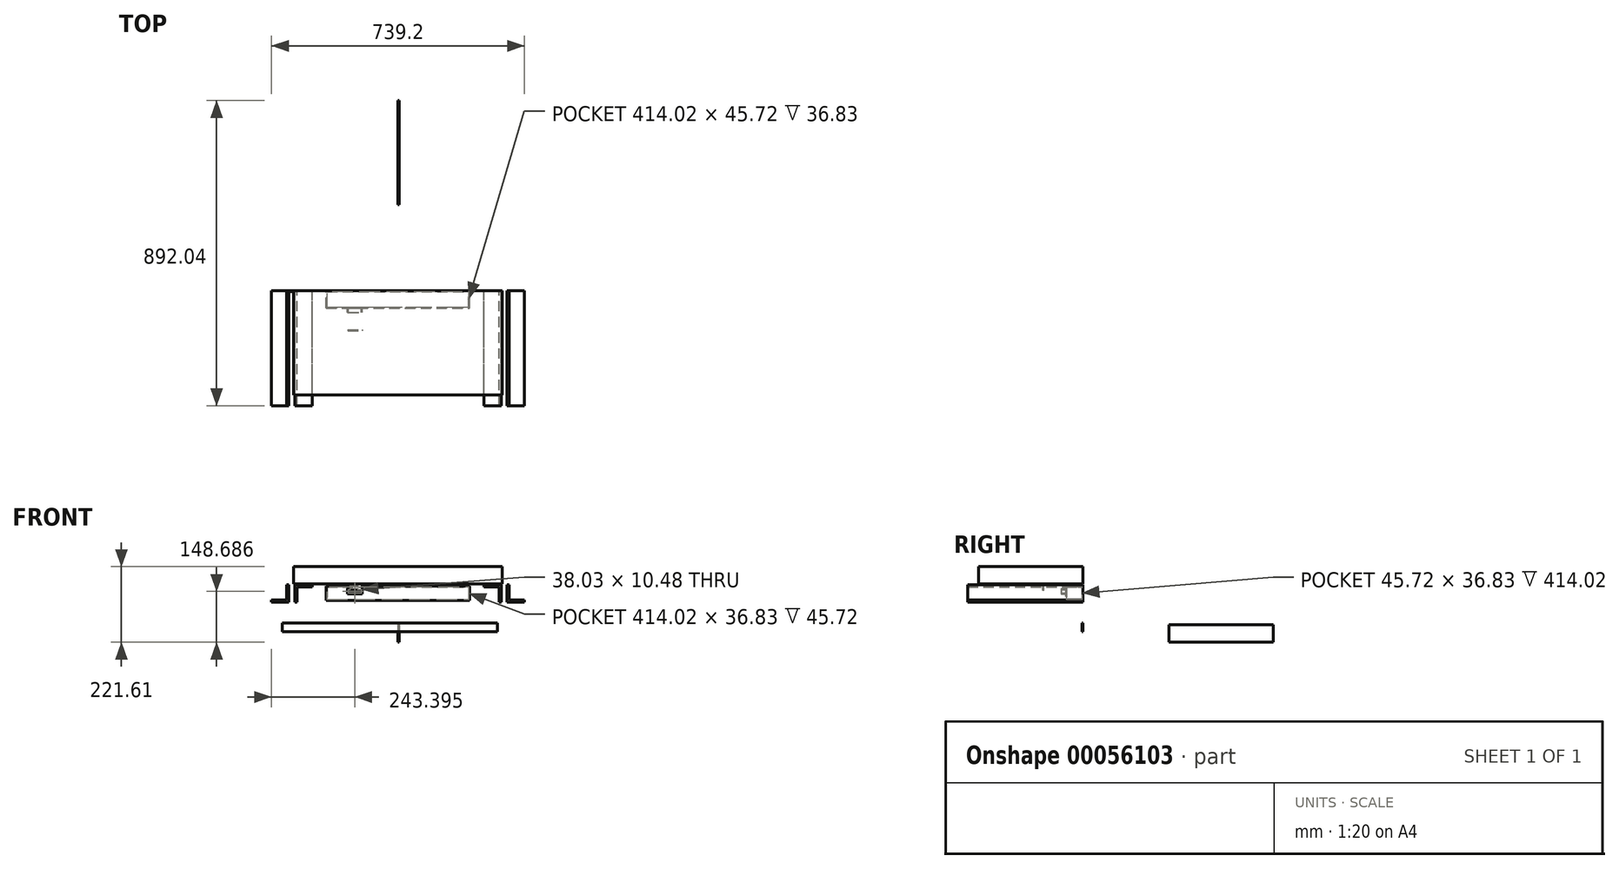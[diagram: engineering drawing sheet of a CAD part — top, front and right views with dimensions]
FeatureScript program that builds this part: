
annotation { "Feature Type Name" : "Feature", "Feature Type Description" : "" }
export const myFeature = defineFeature(function(context is Context, id is Id, definition is map)
    precondition{}
    {
        {
            var Q0;
            Q0=qCreatedBy(makeId("Front.planeOp"),FACE);
            var sketch = newSketch(context, id + "F0", { "sketchPlane" : qUnion([Q0])});
            skLineSegment(sketch, "E0.bottom", {"start": v(-304.8, 110.14) * mm, "end": v(304.8, 110.14) * mm});
            skLineSegment(sketch, "E0.top", {"start": v(-304.8, 59.34) * mm, "end": v(304.8, 59.34) * mm});
            skLineSegment(sketch, "E0.left", {"start": v(-304.8, 110.14) * mm, "end": v(-304.8, 59.34) * mm});
            skLineSegment(sketch, "E0.right", {"start": v(304.8, 110.14) * mm, "end": v(304.8, 59.34) * mm});
            skLineSegment(sketch, "E1.bottom", {"start": v(-209.55, 53) * mm, "end": v(209.55, 53) * mm});
            skLineSegment(sketch, "E1.top", {"start": v(-209.55, 11.08) * mm, "end": v(209.55, 11.08) * mm});
            skLineSegment(sketch, "E1.left", {"start": v(-209.55, 53) * mm, "end": v(-209.55, 11.08) * mm});
            skLineSegment(sketch, "E1.right", {"start": v(209.55, 53) * mm, "end": v(209.55, 11.08) * mm});
            skLineSegment(sketch, "E2", {"start": v(0, 0) * mm, "end": v(0, 201) * mm, "construction": true});
            skLineSegment(sketch, "E3", {"start": v(397.2, 0) * mm, "end": v(-209.55, 0) * mm, "construction": true});
            skSolve(sketch);
        }
        {
            var Q0;
            Q0=makeQuery(id+"F0.imprint","IMPRINT",FACE,{"disambiguationData":[TD([[makeQuery(id+"F0.imprint","IMPRINT",EDGE,{"derivedFrom":sQuery(id+"F0.wireOp",EDGE,"E1.bottom")}),-1.0]])]});
            extrude(context, id + "F1", {"entities" : qUnion([Q0]), "depth" : 50.8 * mm});
        }
        {
            var Q0;
            Q0=makeQuery(id+"F0.imprint","IMPRINT",FACE,{"disambiguationData":[TD([[makeQuery(id+"F0.imprint","IMPRINT",EDGE,{"derivedFrom":sQuery(id+"F0.wireOp",EDGE,"E0.bottom")}),-1.0]])]});
            extrude(context, id + "F2", {"entities" : qUnion([Q0]), "depth" : 304.8 * mm});
        }
        {
            var Q0;
            Q0=qCreatedBy(makeId("Front.planeOp"),FACE);
            var sketch = newSketch(context, id + "F3", { "sketchPlane" : qUnion([Q0])});
            skLineSegment(sketch, "E4", {"start": v(-342.89, 0) * mm, "end": v(465.36, 0) * mm, "construction": true});
            skLineSegment(sketch, "E5", {"start": v(0, -121.63) * mm, "end": v(0, 322.71) * mm, "construction": true});
            skLineSegment(sketch, "E6", {"start": v(250.8, 57.32) * mm, "end": v(301.6, 57.32) * mm});
            skLineSegment(sketch, "E7", {"start": v(301.6, 57.32) * mm, "end": v(301.6, 6.52) * mm});
            skLineSegment(sketch, "E8", {"start": v(301.6, 6.52) * mm, "end": v(295.24, 6.52) * mm});
            skLineSegment(sketch, "E9", {"start": v(295.24, 6.52) * mm, "end": v(295.24, 50.97) * mm});
            skLineSegment(sketch, "E10", {"start": v(295.24, 50.97) * mm, "end": v(250.8, 50.97) * mm});
            skLineSegment(sketch, "E11", {"start": v(250.8, 50.97) * mm, "end": v(250.8, 57.32) * mm});
            skLineSegment(sketch, "E12", {"start": v(318.8, 57.32) * mm, "end": v(318.8, 6.52) * mm});
            skLineSegment(sketch, "E13", {"start": v(318.8, 6.52) * mm, "end": v(369.6, 6.52) * mm});
            skLineSegment(sketch, "E14", {"start": v(369.6, 6.52) * mm, "end": v(369.6, 12.87) * mm});
            skLineSegment(sketch, "E15", {"start": v(369.6, 12.87) * mm, "end": v(325.15, 12.87) * mm});
            skLineSegment(sketch, "E16", {"start": v(325.15, 12.87) * mm, "end": v(325.15, 57.32) * mm});
            skLineSegment(sketch, "E17", {"start": v(325.15, 57.32) * mm, "end": v(318.8, 57.32) * mm});
            skLineSegment(sketch, "E18.MirrorCS", {"start": v(-325.15, 57.32) * mm, "end": v(-318.8, 57.32) * mm});
            skLineSegment(sketch, "E19.MirrorCS", {"start": v(-250.8, 50.97) * mm, "end": v(-250.8, 57.32) * mm});
            skLineSegment(sketch, "E20.MirrorCS", {"start": v(-325.15, 12.87) * mm, "end": v(-325.15, 57.32) * mm});
            skLineSegment(sketch, "E21.MirrorCS", {"start": v(-250.8, 57.32) * mm, "end": v(-301.6, 57.32) * mm});
            skLineSegment(sketch, "E22.MirrorCS", {"start": v(-301.6, 57.32) * mm, "end": v(-301.6, 6.52) * mm});
            skLineSegment(sketch, "E23.MirrorCS", {"start": v(-318.8, 57.32) * mm, "end": v(-318.8, 6.52) * mm});
            skLineSegment(sketch, "E24.MirrorCS", {"start": v(-301.6, 6.52) * mm, "end": v(-295.24, 6.52) * mm});
            skLineSegment(sketch, "E25.MirrorCS", {"start": v(-369.6, 6.52) * mm, "end": v(-369.6, 12.87) * mm});
            skLineSegment(sketch, "E26.MirrorCS", {"start": v(-369.6, 12.87) * mm, "end": v(-325.15, 12.87) * mm});
            skLineSegment(sketch, "E27.MirrorCS", {"start": v(-295.24, 6.52) * mm, "end": v(-295.24, 50.97) * mm});
            skLineSegment(sketch, "E28.MirrorCS", {"start": v(-318.8, 6.52) * mm, "end": v(-369.6, 6.52) * mm});
            skLineSegment(sketch, "E29.MirrorCS", {"start": v(-295.24, 50.97) * mm, "end": v(-250.8, 50.97) * mm});
            skSolve(sketch);
        }
        {
            var Q0;
            Q0=makeQuery(id+"F3.imprint","IMPRINT",FACE,{"disambiguationData":[TD([[makeQuery(id+"F3.imprint","IMPRINT",EDGE,{"derivedFrom":sQuery(id+"F3.wireOp",EDGE,"E6")}),-1.0]])]});
            var Q1;
            Q1=makeQuery(id+"F3.imprint","IMPRINT",FACE,{"disambiguationData":[TD([[makeQuery(id+"F3.imprint","IMPRINT",EDGE,{"derivedFrom":sQuery(id+"F3.wireOp",EDGE,"E12")}),1.0]])]});
            extrude(context, id + "F4", {"entities" : qUnion([Q0, Q1]), "operationType" : NewBodyOperationType.ADD, "depth" : 336.55 * mm});
        }
        {
            var Q0;
            Q0 = qSketchRegion(id + "F3", true);
            extrude(context, id + "F5", {"entities" : qUnion([Q0]), "depth" : 336.55 * mm});
        }
        {
            var Q0;
            Q0=makeQuery(id+"F1.opExtrude","CAP_FACE",FACE,{"disambiguationData":[OSD([sQuery(id+"F0.wireOp",EDGE,"E1.bottom"),sQuery(id+"F0.wireOp",EDGE,"E1.top"),sQuery(id+"F0.wireOp",EDGE,"E1.left"),sQuery(id+"F0.wireOp",EDGE,"E1.right")])],"isStart":false});
            var sketch = newSketch(context, id + "F6", { "sketchPlane" : qUnion([Q0])});
            skLineSegment(sketch, "E30.bottom", {"start": v(-147.76, 45) * mm, "end": v(-104.65, 45) * mm});
            skLineSegment(sketch, "E30.top", {"start": v(-147.76, 29.44) * mm, "end": v(-104.65, 29.44) * mm});
            skLineSegment(sketch, "E30.left", {"start": v(-147.76, 45) * mm, "end": v(-147.76, 29.44) * mm});
            skLineSegment(sketch, "E30.right", {"start": v(-104.65, 45) * mm, "end": v(-104.65, 29.44) * mm});
            skSolve(sketch);
        }
        {
            var Q0;
            Q0 = qSketchRegion(id + "F6", true);
            extrude(context, id + "F7", {"entities" : qUnion([Q0]), "operationType" : NewBodyOperationType.ADD, "depth" : 12.7 * mm});
        }
        {
            var Q0;
            Q0=makeQuery(id+"F7.opExtrude","CAP_FACE",FACE,{"disambiguationData":[OSD([sQuery(id+"F6.wireOp",EDGE,"E30.bottom"),sQuery(id+"F6.wireOp",EDGE,"E30.top"),sQuery(id+"F6.wireOp",EDGE,"E30.left"),sQuery(id+"F6.wireOp",EDGE,"E30.right")])],"isStart":false});
            shell(context, id + "F8", {"entities" : qUnion([Q0]), "thickness" : 2.54 * mm});
        }
        {
            var Q0;
            Q0=makeQuery(id+"F2.opExtrude","SWEPT_FACE",FACE,{"disambiguationData":[OSD([sQuery(id+"F0.wireOp",EDGE,"E0.top")])]});
            var sketch = newSketch(context, id + "F9", { "sketchPlane" : qUnion([Q0])});
            skLineSegment(sketch, "E31.bottom", {"start": v(-146.45, 114.37) * mm, "end": v(-104.72, 114.37) * mm});
            skLineSegment(sketch, "E31.top", {"start": v(-146.45, 142.56) * mm, "end": v(-104.72, 142.56) * mm});
            skLineSegment(sketch, "E31.left", {"start": v(-146.45, 114.37) * mm, "end": v(-146.45, 142.56) * mm});
            skLineSegment(sketch, "E31.right", {"start": v(-104.72, 114.37) * mm, "end": v(-104.72, 142.56) * mm});
            skSolve(sketch);
        }
        {
            var Q0;
            Q0=makeQuery(id+"F9.imprint","IMPRINT",FACE,{"disambiguationData":[TD([[makeQuery(id+"F9.imprint","IMPRINT",EDGE,{"derivedFrom":sQuery(id+"F9.wireOp",EDGE,"E31.bottom")}),1.0]])]});
            extrude(context, id + "F10", {"entities" : qUnion([Q0]), "depth" : 19.05 * mm});
        }
        {
            var Q0;
            Q0=makeQuery(id+"F10.opExtrude","SWEPT_FACE",FACE,{"disambiguationData":[OSD([sQuery(id+"F9.wireOp",EDGE,"E31.top")])]});
            var sketch = newSketch(context, id + "F11", { "sketchPlane" : qUnion([Q0])});
            skLineSegment(sketch, "E32", {"start": v(-146.45, 59.34) * mm, "end": v(-125.59, 40.3) * mm});
            skLineSegment(sketch, "E33", {"start": v(-104.72, 59.34) * mm, "end": v(-125.59, 40.3) * mm});
            skLineSegment(sketch, "E34", {"start": v(-125.59, 59.34) * mm, "end": v(-125.59, -27.4) * mm, "construction": true});
            skSolve(sketch);
        }
        {
            var Q0;
            {var subQ0=sQuery(id+"F11.wireOp",EDGE,"E33");Q0=makeQuery(id+"F11.imprint","IMPRINT",FACE,{"disambiguationData":[TD([[makeQuery(id+"F11.imprint","IMPRINT",EDGE,{"derivedFrom":subQ0}),1.0]])]});}
            var Q1;
            {var subQ0=sQuery(id+"F11.wireOp",EDGE,"E32");Q1=makeQuery(id+"F11.imprint","IMPRINT",FACE,{"disambiguationData":[TD([[makeQuery(id+"F11.imprint","IMPRINT",EDGE,{"derivedFrom":subQ0}),-1.0]])]});}
            var Q2;
            Q2=makeQuery(id+"F11.imprint","IMPRINT",FACE,{"disambiguationData":[TD([[makeQuery(id+"F11.imprint","IMPRINT",EDGE,{"derivedFrom":sQuery(id+"F11.wireOp",EDGE,"E32")}),1.0]])]});
            extrude(context, id + "F12", {"entities" : qUnion([Q0, Q1, Q2]), "operationType" : NewBodyOperationType.REMOVE, "oppositeDirection" : true, "depth" : 25.4 * mm});
        }
        {
            var Q0;
            Q0=qCreatedBy(makeId("Right.planeOp"),FACE);
            var sketch = newSketch(context, id + "F13", { "sketchPlane" : qUnion([Q0])});
            skLineSegment(sketch, "E35.bottom", {"start": v(555.5, -60.67) * mm, "end": v(250.7, -60.67) * mm});
            skLineSegment(sketch, "E35.top", {"start": v(555.5, -111.47) * mm, "end": v(250.7, -111.47) * mm});
            skLineSegment(sketch, "E35.left", {"start": v(555.5, -60.67) * mm, "end": v(555.5, -111.47) * mm});
            skLineSegment(sketch, "E35.right", {"start": v(250.7, -60.67) * mm, "end": v(250.7, -111.47) * mm});
            skSolve(sketch);
        }
        {
            var Q0;
            Q0=makeQuery(id+"F13.imprint","IMPRINT",FACE,{"disambiguationData":[TD([[makeQuery(id+"F13.imprint","IMPRINT",EDGE,{"derivedFrom":sQuery(id+"F13.wireOp",EDGE,"E35.bottom")}),1.0]])]});
            extrude(context, id + "F14", {"entities" : qUnion([Q0]), "depth" : 3.17 * mm});
        }
        {
            var Q0;
            Q0=qCreatedBy(makeId("Front.planeOp"),FACE);
            var sketch = newSketch(context, id + "F15", { "sketchPlane" : qUnion([Q0])});
            skLineSegment(sketch, "E36.bottom", {"start": v(290.98, -55.66) * mm, "end": v(-337.67, -55.66) * mm});
            skLineSegment(sketch, "E36.top", {"start": v(290.98, -81.06) * mm, "end": v(-337.67, -81.06) * mm});
            skLineSegment(sketch, "E36.left", {"start": v(290.98, -55.66) * mm, "end": v(290.98, -81.06) * mm});
            skLineSegment(sketch, "E36.right", {"start": v(-337.67, -55.66) * mm, "end": v(-337.67, -81.06) * mm});
            skSolve(sketch);
        }
        {
            var Q0;
            Q0=makeQuery(id+"F15.imprint","IMPRINT",FACE,{"disambiguationData":[TD([[makeQuery(id+"F15.imprint","IMPRINT",EDGE,{"derivedFrom":sQuery(id+"F15.wireOp",EDGE,"E36.bottom")}),1.0]])]});
            extrude(context, id + "F16", {"entities" : qUnion([Q0]), "depth" : 3.17 * mm});
        }
    });
